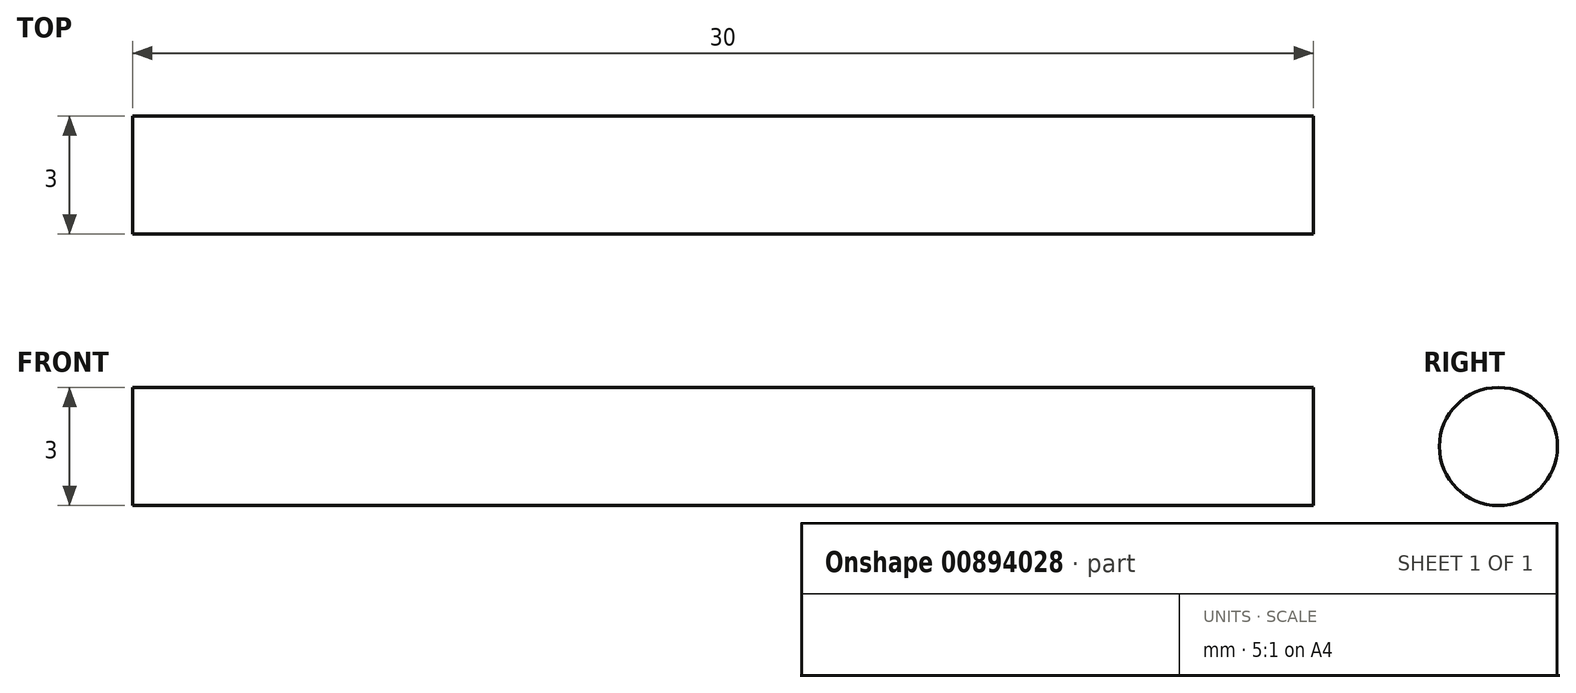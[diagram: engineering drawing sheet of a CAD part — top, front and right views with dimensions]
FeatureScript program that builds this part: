
annotation { "Feature Type Name" : "Feature", "Feature Type Description" : "" }
export const myFeature = defineFeature(function(context is Context, id is Id, definition is map)
    precondition{}
    {
        {
            var Q0;
            Q0=qCreatedBy(makeId("Right.planeOp"),FACE);
            var sketch = newSketch(context, id + "F0", { "sketchPlane" : qUnion([Q0])});
            skCircle(sketch, "E0", {"center": v(-3.78, 21.33) * mm, "radius": 1.5 * mm});
            skSolve(sketch);
        }
        {
            var Q0;
            Q0=makeQuery(id+"F0.imprint","IMPRINT",FACE,{"disambiguationData":[TD([[makeQuery(id+"F0.imprint","IMPRINT",EDGE,{"derivedFrom":sQuery(id+"F0.wireOp",EDGE,"E0")}),1.0]])]});
            extrude(context, id + "F1", {"entities" : qUnion([Q0]), "depth" : 30 * mm, "offsetDistance" : 25 * mm});
        }
    });
